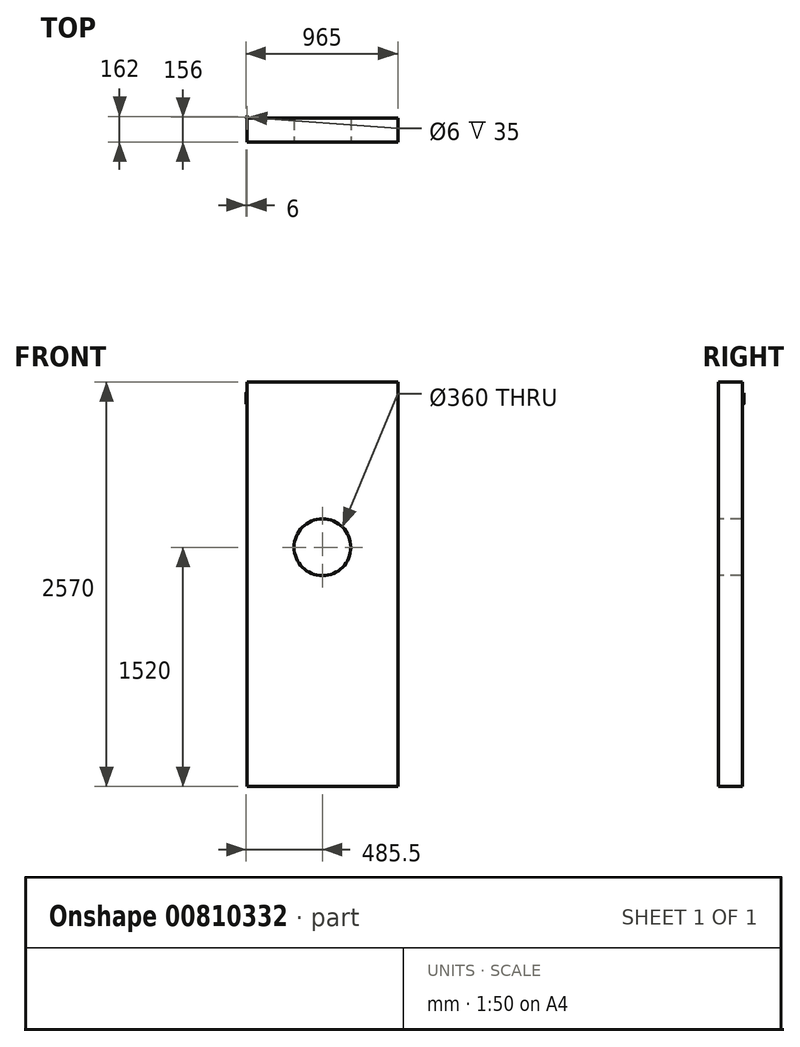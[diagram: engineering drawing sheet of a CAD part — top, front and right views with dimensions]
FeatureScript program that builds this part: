
annotation { "Feature Type Name" : "Feature", "Feature Type Description" : "" }
export const myFeature = defineFeature(function(context is Context, id is Id, definition is map)
    precondition{}
    {
        {
            var Q0;
            Q0=qCreatedBy(makeId("Front.planeOp"),FACE);
            var sketch = newSketch(context, id + "F0", { "sketchPlane" : qUnion([Q0])});
            skLineSegment(sketch, "E0.bottom", {"start": v(-479.5, 1285) * mm, "end": v(479.5, 1285) * mm});
            skLineSegment(sketch, "E0.left", {"start": v(-479.5, 1285) * mm, "end": v(-479.5, -1285) * mm});
            skLineSegment(sketch, "E0.right", {"start": v(479.5, 1285) * mm, "end": v(479.5, -1285) * mm});
            skLineSegment(sketch, "E1", {"start": v(0, 1410.47) * mm, "end": v(0, -2114.9) * mm, "construction": true});
            skLineSegment(sketch, "E2", {"start": v(-1789.88, 0) * mm, "end": v(2687.12, 0) * mm, "construction": true});
            skLineSegment(sketch, "E3", {"start": v(-479.5, -1285) * mm, "end": v(479.5, -1285) * mm});
            skSolve(sketch);
        }
        {
            var Q0;
            Q0 = qSketchRegion(id + "F0", true);
            extrude(context, id + "F1", {"entities" : qUnion([Q0]), "depth" : 150 * mm, "offsetDistance" : 25.4 * mm});
        }
        {
            var Q0;
            Q0=makeQuery(id+"F1.opExtrude","CAP_FACE",FACE,{"disambiguationData":[OSD([sQuery(id+"F0.wireOp",EDGE,"E0.bottom"),sQuery(id+"F0.wireOp",EDGE,"E0.left"),sQuery(id+"F0.wireOp",EDGE,"E0.right"),sQuery(id+"F0.wireOp",EDGE,"E3")])],"isStart":false});
            var sketch = newSketch(context, id + "F2", { "sketchPlane" : qUnion([Q0])});
            skCircle(sketch, "E4", {"center": v(0, 235) * mm, "radius": 180 * mm});
            skSolve(sketch);
        }
        {
            var Q0;
            Q0 = qSketchRegion(id + "F2", true);
            extrude(context, id + "F3", {"entities" : qUnion([Q0]), "operationType" : NewBodyOperationType.REMOVE, "oppositeDirection" : true, "depth" : 185.42 * mm, "offsetDistance" : 25.4 * mm});
        }
        {
            var Q0;
            Q0=makeQuery(id+"F1.opExtrude","SWEPT_FACE",FACE,{"disambiguationData":[OSD([sQuery(id+"F0.wireOp",EDGE,"E0.bottom")])]});
            cPlane(context, id + "F4", {"entities" : qUnion([Q0]), "cplaneType" : CPlaneType.OFFSET, "offset" : 70 * mm, "oppositeDirection" : true, "width" : 152.4 * mm, "height" : 152.4 * mm});
        }
        {
            var Q0;
            Q0=qCreatedBy(id+"F4.planeOp",FACE);
            var sketch = newSketch(context, id + "F5", { "sketchPlane" : qUnion([Q0])});
            skCircle(sketch, "E5", {"center": v(-479.5, 6) * mm, "radius": 6 * mm});
            skSolve(sketch);
        }
        {
            var Q0;
            Q0 = qSketchRegion(id + "F5", true);
            extrude(context, id + "F6", {"entities" : qUnion([Q0]), "oppositeDirection" : true, "depth" : 70 * mm, "offsetDistance" : 25.4 * mm});
        }
        {
            var Q0;
            Q0=makeQuery(id+"F6.opExtrude","CAP_FACE",FACE,{"disambiguationData":[OSD([sQuery(id+"F5.wireOp",EDGE,"E5")])],"isStart":false});
            var sketch = newSketch(context, id + "F7", { "sketchPlane" : qUnion([Q0])});
            skCircle(sketch, "E6", {"center": v(-479.5, -6) * mm, "radius": 3 * mm});
            skSolve(sketch);
        }
        {
            var Q0;
            Q0 = qSketchRegion(id + "F7", true);
            extrude(context, id + "F8", {"entities" : qUnion([Q0]), "operationType" : NewBodyOperationType.REMOVE, "oppositeDirection" : true, "depth" : 35 * mm, "offsetDistance" : 25.4 * mm});
        }
    });
